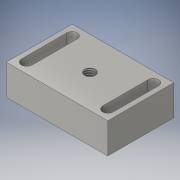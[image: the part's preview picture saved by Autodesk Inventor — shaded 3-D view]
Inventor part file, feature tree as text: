
AUTODESK INVENTOR PART (.ipt)
format: ipt  version: 2016 (Build 200138000, 138)  size: 123,904 bytes
history: native  units: in
note: dims shown in document units (in); Inventor stores cm internally (conversion verified against a paired STEP export)
features: sketch x3, extrude x2, hole x1
ambient origin geometry x8: Origin, YZ Plane, XZ Plane, XY Plane, X Axis, Y Axis, Z Axis, Center Point
bodies: Solid1 (feature_tree)
feature tree (6):
  extrude  "Stock Block"  Depth=2.5in
  hole  "Mounting Hole"  [1 undecoded]
  extrude  "Slots"  Depth=0.26in
  sketch  "Sketch1"  dims[d0=1.625in d1=0.0in d2=2.5in]
  sketch  "Sketch2"  dims[d3=0.75in d4=0.8125in]
  sketch  "Sketch3"  dims[d5=1.25in d6=0.262in d7=0.63in d8=0.375in d9=0.25in d10=0.5635in d11=0.874in d12=0.8108in d13=0.26in d15=0.125in d16=0.125in d18=1.0in d19=0.0in d24=1.0in]
note: 1 required parameter value undecoded (feature->parameter linkage not recoverable at this tier; creation-order binding heuristic only, values carry confidence <= 0.55)
